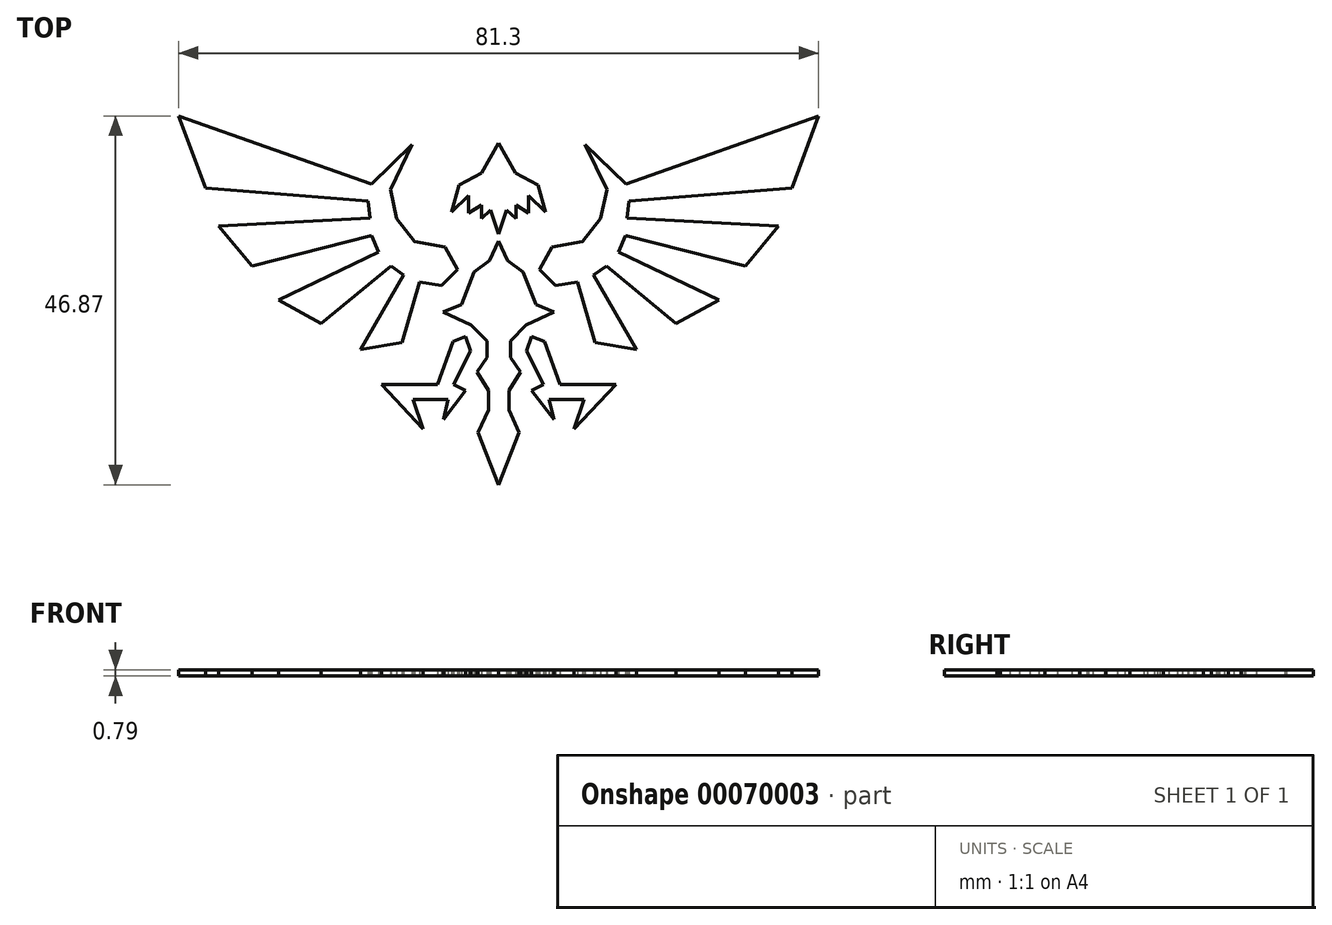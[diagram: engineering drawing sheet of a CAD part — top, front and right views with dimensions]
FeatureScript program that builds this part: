
annotation { "Feature Type Name" : "Feature", "Feature Type Description" : "" }
export const myFeature = defineFeature(function(context is Context, id is Id, definition is map)
    precondition{}
    {
        {
            var Q0;
            Q0=qCreatedBy(makeId("Top.planeOp"),FACE);
            var sketch = newSketch(context, id + "F0", { "sketchPlane" : qUnion([Q0])});
            skLineSegment(sketch, "E0", {"start": v(0, 20.5) * mm, "end": v(-2.15, 16.68) * mm});
            skLineSegment(sketch, "E1", {"start": v(-2.15, 16.68) * mm, "end": v(-5.02, 15.14) * mm});
            skLineSegment(sketch, "E2", {"start": v(-5.02, 15.14) * mm, "end": v(-5.97, 11.7) * mm});
            skLineSegment(sketch, "E3", {"start": v(-5.97, 11.7) * mm, "end": v(-3.82, 13.8) * mm});
            skLineSegment(sketch, "E4", {"start": v(-3.82, 13.8) * mm, "end": v(-3.82, 11.58) * mm});
            skLineSegment(sketch, "E5", {"start": v(-3.82, 11.58) * mm, "end": v(-2.2, 12.6) * mm});
            skLineSegment(sketch, "E6", {"start": v(-2.2, 12.6) * mm, "end": v(-2.2, 10.9) * mm});
            skLineSegment(sketch, "E7", {"start": v(-2.2, 10.9) * mm, "end": v(-1.04, 11.96) * mm});
            skLineSegment(sketch, "E8", {"start": v(-1.04, 11.96) * mm, "end": v(0, 8.96) * mm});
            skLineSegment(sketch, "E9", {"start": v(0, 8.08) * mm, "end": v(-1.16, 5.56) * mm});
            skLineSegment(sketch, "E10", {"start": v(-1.16, 5.56) * mm, "end": v(-3.1, 4.13) * mm});
            skLineSegment(sketch, "E11", {"start": v(-3.1, 4.13) * mm, "end": v(-4.73, 0) * mm});
            skLineSegment(sketch, "E12", {"start": v(-4.73, 0) * mm, "end": v(-7.05, -0.94) * mm});
            skLineSegment(sketch, "E13", {"start": v(-7.05, -0.94) * mm, "end": v(-3.48, -2.6) * mm});
            skLineSegment(sketch, "E14", {"start": v(-3.48, -2.6) * mm, "end": v(-1.5, -4.67) * mm});
            skLineSegment(sketch, "E15", {"start": v(-1.5, -4.67) * mm, "end": v(-1.5, -6.75) * mm});
            skLineSegment(sketch, "E16", {"start": v(-1.5, -6.75) * mm, "end": v(-2.76, -8.59) * mm});
            skLineSegment(sketch, "E17", {"start": v(-2.76, -8.59) * mm, "end": v(-1.3, -10.94) * mm});
            skLineSegment(sketch, "E18", {"start": v(-1.3, -10.94) * mm, "end": v(-1.3, -13.44) * mm});
            skLineSegment(sketch, "E19", {"start": v(-1.3, -13.44) * mm, "end": v(-2.6, -16.26) * mm});
            skLineSegment(sketch, "E20", {"start": v(-2.6, -16.26) * mm, "end": v(0, -22.92) * mm});
            skLineSegment(sketch, "E21", {"start": v(-7.78, -10.17) * mm, "end": v(-5.8, -4.72) * mm});
            skLineSegment(sketch, "E22", {"start": v(-5.8, -4.72) * mm, "end": v(-4.17, -4.1) * mm});
            skLineSegment(sketch, "E23", {"start": v(-4.17, -4.1) * mm, "end": v(-3.54, -5.9) * mm});
            skLineSegment(sketch, "E24", {"start": v(-3.54, -5.9) * mm, "end": v(-5.72, -10.17) * mm});
            skLineSegment(sketch, "E25", {"start": v(-5.72, -10.17) * mm, "end": v(-4.2, -10.96) * mm});
            skLineSegment(sketch, "E26", {"start": v(-4.2, -10.96) * mm, "end": v(-7.01, -14.62) * mm});
            skLineSegment(sketch, "E27", {"start": v(-7.01, -14.62) * mm, "end": v(-6.43, -12.1) * mm});
            skLineSegment(sketch, "E28", {"start": v(-6.43, -12.1) * mm, "end": v(-10.86, -12.1) * mm});
            skLineSegment(sketch, "E29", {"start": v(-10.86, -12.1) * mm, "end": v(-9.58, -15.85) * mm});
            skLineSegment(sketch, "E30", {"start": v(-9.58, -15.85) * mm, "end": v(-14.88, -10.17) * mm});
            skLineSegment(sketch, "E31", {"start": v(-14.88, -10.17) * mm, "end": v(-7.78, -10.17) * mm});
            skLineSegment(sketch, "E32", {"start": v(-12.95, 10.93) * mm, "end": v(-13.75, 14.56) * mm});
            skLineSegment(sketch, "E33", {"start": v(-13.75, 14.56) * mm, "end": v(-10.98, 20.31) * mm});
            skLineSegment(sketch, "E34", {"start": v(-10.98, 20.31) * mm, "end": v(-16.15, 15.28) * mm});
            skLineSegment(sketch, "E35", {"start": v(-16.15, 15.28) * mm, "end": v(-40.65, 23.95) * mm});
            skLineSegment(sketch, "E36", {"start": v(-40.65, 23.95) * mm, "end": v(-37.26, 14.76) * mm});
            skLineSegment(sketch, "E37", {"start": v(-37.26, 14.76) * mm, "end": v(-16.57, 13.15) * mm});
            skLineSegment(sketch, "E38", {"start": v(-16.57, 13.15) * mm, "end": v(-16.33, 10.94) * mm});
            skLineSegment(sketch, "E39", {"start": v(-16.33, 10.94) * mm, "end": v(-35.56, 9.93) * mm});
            skLineSegment(sketch, "E40", {"start": v(-35.56, 9.93) * mm, "end": v(-31.33, 4.86) * mm});
            skLineSegment(sketch, "E41", {"start": v(-31.33, 4.86) * mm, "end": v(-16.11, 8.76) * mm});
            skLineSegment(sketch, "E42", {"start": v(-16.11, 8.76) * mm, "end": v(-15.25, 6.65) * mm});
            skLineSegment(sketch, "E43", {"start": v(-15.25, 6.65) * mm, "end": v(-27.97, 0.59) * mm});
            skLineSegment(sketch, "E44", {"start": v(-27.97, 0.59) * mm, "end": v(-22.55, -2.43) * mm});
            skLineSegment(sketch, "E45", {"start": v(-22.55, -2.43) * mm, "end": v(-13.69, 4.9) * mm});
            skLineSegment(sketch, "E46", {"start": v(-13.69, 4.9) * mm, "end": v(-12.06, 3.72) * mm});
            skLineSegment(sketch, "E47", {"start": v(-12.06, 3.72) * mm, "end": v(-17.53, -5.7) * mm});
            skLineSegment(sketch, "E48", {"start": v(-17.53, -5.7) * mm, "end": v(-12.27, -4.85) * mm});
            skLineSegment(sketch, "E49", {"start": v(-12.27, -4.85) * mm, "end": v(-10.05, 2.84) * mm});
            skLineSegment(sketch, "E50", {"start": v(-10.05, 2.84) * mm, "end": v(-7.24, 2.41) * mm});
            skLineSegment(sketch, "E51", {"start": v(-7.24, 2.41) * mm, "end": v(-5.21, 4.44) * mm});
            skLineSegment(sketch, "E52", {"start": v(-5.21, 4.44) * mm, "end": v(-6.79, 7.27) * mm});
            skLineSegment(sketch, "E53", {"start": v(0, 33.15) * mm, "end": v(0, -4.67) * mm, "construction": true});
            skLineSegment(sketch, "E54.MirrorCS", {"start": v(1.3, -10.94) * mm, "end": v(1.3, -13.44) * mm});
            skLineSegment(sketch, "E55.MirrorCS", {"start": v(5.8, -4.72) * mm, "end": v(4.17, -4.1) * mm});
            skLineSegment(sketch, "E56.MirrorCS", {"start": v(13.69, 4.9) * mm, "end": v(12.06, 3.72) * mm});
            skLineSegment(sketch, "E57.MirrorCS", {"start": v(4.73, 0) * mm, "end": v(7.05, -0.94) * mm});
            skLineSegment(sketch, "E58.MirrorCS", {"start": v(5.72, -10.17) * mm, "end": v(4.2, -10.96) * mm});
            skLineSegment(sketch, "E59.MirrorCS", {"start": v(1.16, 5.56) * mm, "end": v(3.1, 4.13) * mm});
            skLineSegment(sketch, "E60.MirrorCS", {"start": v(7.01, -14.62) * mm, "end": v(6.43, -12.1) * mm});
            skLineSegment(sketch, "E61.MirrorCS", {"start": v(16.11, 8.76) * mm, "end": v(15.25, 6.65) * mm});
            skLineSegment(sketch, "E62.MirrorCS", {"start": v(3.82, 13.8) * mm, "end": v(3.82, 11.58) * mm});
            skLineSegment(sketch, "E63.MirrorCS", {"start": v(5.97, 11.7) * mm, "end": v(3.82, 13.8) * mm});
            skLineSegment(sketch, "E64.MirrorCS", {"start": v(3.82, 11.58) * mm, "end": v(2.2, 12.6) * mm});
            skLineSegment(sketch, "E65.MirrorCS", {"start": v(1.5, -6.75) * mm, "end": v(2.76, -8.59) * mm});
            skLineSegment(sketch, "E66.MirrorCS", {"start": v(2.2, 10.9) * mm, "end": v(1.04, 11.96) * mm});
            skLineSegment(sketch, "E67.MirrorCS", {"start": v(2.76, -8.59) * mm, "end": v(1.3, -10.94) * mm});
            skLineSegment(sketch, "E68.MirrorCS", {"start": v(2.2, 12.6) * mm, "end": v(2.2, 10.9) * mm});
            skLineSegment(sketch, "E69.MirrorCS", {"start": v(7.24, 2.41) * mm, "end": v(5.21, 4.44) * mm});
            skLineSegment(sketch, "E70.MirrorCS", {"start": v(1.5, -4.67) * mm, "end": v(1.5, -6.75) * mm});
            skLineSegment(sketch, "E71.MirrorCS", {"start": v(16.57, 13.15) * mm, "end": v(16.33, 10.94) * mm});
            skLineSegment(sketch, "E72.MirrorCS", {"start": v(4.17, -4.1) * mm, "end": v(3.54, -5.9) * mm});
            skLineSegment(sketch, "E73.MirrorCS", {"start": v(3.48, -2.6) * mm, "end": v(1.5, -4.67) * mm});
            skLineSegment(sketch, "E74.MirrorCS", {"start": v(4.2, -10.96) * mm, "end": v(7.01, -14.62) * mm});
            skLineSegment(sketch, "E75.MirrorCS", {"start": v(10.05, 2.84) * mm, "end": v(7.24, 2.41) * mm});
            skLineSegment(sketch, "E76.MirrorCS", {"start": v(10.98, 20.31) * mm, "end": v(16.15, 15.28) * mm});
            skLineSegment(sketch, "E77.MirrorCS", {"start": v(1.3, -13.44) * mm, "end": v(2.6, -16.26) * mm});
            skLineSegment(sketch, "E78.MirrorCS", {"start": v(13.75, 14.56) * mm, "end": v(10.98, 20.31) * mm});
            skLineSegment(sketch, "E79.MirrorCS", {"start": v(12.27, -4.85) * mm, "end": v(10.05, 2.84) * mm});
            skLineSegment(sketch, "E80.MirrorCS", {"start": v(14.88, -10.17) * mm, "end": v(7.78, -10.17) * mm});
            skLineSegment(sketch, "E81.MirrorCS", {"start": v(37.26, 14.76) * mm, "end": v(16.57, 13.15) * mm});
            skLineSegment(sketch, "E82.MirrorCS", {"start": v(15.25, 6.65) * mm, "end": v(27.97, 0.59) * mm});
            skLineSegment(sketch, "E83.MirrorCS", {"start": v(6.43, -12.1) * mm, "end": v(10.86, -12.1) * mm});
            skLineSegment(sketch, "E84.MirrorCS", {"start": v(3.54, -5.9) * mm, "end": v(5.72, -10.17) * mm});
            skLineSegment(sketch, "E85.MirrorCS", {"start": v(16.33, 10.94) * mm, "end": v(35.56, 9.93) * mm});
            skLineSegment(sketch, "E86.MirrorCS", {"start": v(3.1, 4.13) * mm, "end": v(4.73, 0) * mm});
            skLineSegment(sketch, "E87.MirrorCS", {"start": v(22.55, -2.43) * mm, "end": v(13.69, 4.9) * mm});
            skLineSegment(sketch, "E88.MirrorCS", {"start": v(35.56, 9.93) * mm, "end": v(31.33, 4.86) * mm});
            skLineSegment(sketch, "E89.MirrorCS", {"start": v(5.21, 4.44) * mm, "end": v(6.79, 7.27) * mm});
            skLineSegment(sketch, "E90.MirrorCS", {"start": v(9.58, -15.85) * mm, "end": v(14.88, -10.17) * mm});
            skLineSegment(sketch, "E91.MirrorCS", {"start": v(0, 8.08) * mm, "end": v(1.16, 5.56) * mm});
            skLineSegment(sketch, "E92.MirrorCS", {"start": v(1.04, 11.96) * mm, "end": v(0, 8.96) * mm});
            skLineSegment(sketch, "E93.MirrorCS", {"start": v(7.78, -10.17) * mm, "end": v(5.8, -4.72) * mm});
            skLineSegment(sketch, "E94.MirrorCS", {"start": v(40.65, 23.95) * mm, "end": v(37.26, 14.76) * mm});
            skLineSegment(sketch, "E95.MirrorCS", {"start": v(10.86, -12.1) * mm, "end": v(9.58, -15.85) * mm});
            skLineSegment(sketch, "E96.MirrorCS", {"start": v(31.33, 4.86) * mm, "end": v(16.11, 8.76) * mm});
            skLineSegment(sketch, "E97.MirrorCS", {"start": v(12.95, 10.93) * mm, "end": v(13.75, 14.56) * mm});
            skLineSegment(sketch, "E98.MirrorCS", {"start": v(2.6, -16.26) * mm, "end": v(0, -22.92) * mm});
            skLineSegment(sketch, "E99.MirrorCS", {"start": v(17.53, -5.7) * mm, "end": v(12.27, -4.85) * mm});
            skLineSegment(sketch, "E100.MirrorCS", {"start": v(16.15, 15.28) * mm, "end": v(40.65, 23.95) * mm});
            skLineSegment(sketch, "E101.MirrorCS", {"start": v(0, 20.5) * mm, "end": v(2.15, 16.68) * mm});
            skLineSegment(sketch, "E102.MirrorCS", {"start": v(2.15, 16.68) * mm, "end": v(5.02, 15.14) * mm});
            skLineSegment(sketch, "E103.MirrorCS", {"start": v(7.05, -0.94) * mm, "end": v(3.48, -2.6) * mm});
            skLineSegment(sketch, "E104.MirrorCS", {"start": v(12.06, 3.72) * mm, "end": v(17.53, -5.7) * mm});
            skLineSegment(sketch, "E105.MirrorCS", {"start": v(27.97, 0.59) * mm, "end": v(22.55, -2.43) * mm});
            skLineSegment(sketch, "E106.MirrorCS", {"start": v(5.02, 15.14) * mm, "end": v(5.97, 11.7) * mm});
            skLineSegment(sketch, "E107", {"start": v(-12.95, 10.93) * mm, "end": v(-10.66, 8) * mm});
            skLineSegment(sketch, "E108", {"start": v(-10.66, 8) * mm, "end": v(-6.79, 7.27) * mm});
            skLineSegment(sketch, "E109.MirrorCS", {"start": v(12.95, 10.93) * mm, "end": v(10.66, 8) * mm});
            skLineSegment(sketch, "E110.MirrorCS", {"start": v(10.66, 8) * mm, "end": v(6.79, 7.27) * mm});
            skSolve(sketch);
        }
        {
            var Q0;
            Q0 = qSketchRegion(id + "F0", true);
            extrude(context, id + "F1", {"entities" : qUnion([Q0]), "depth" : 0.8 * mm});
        }
    });
